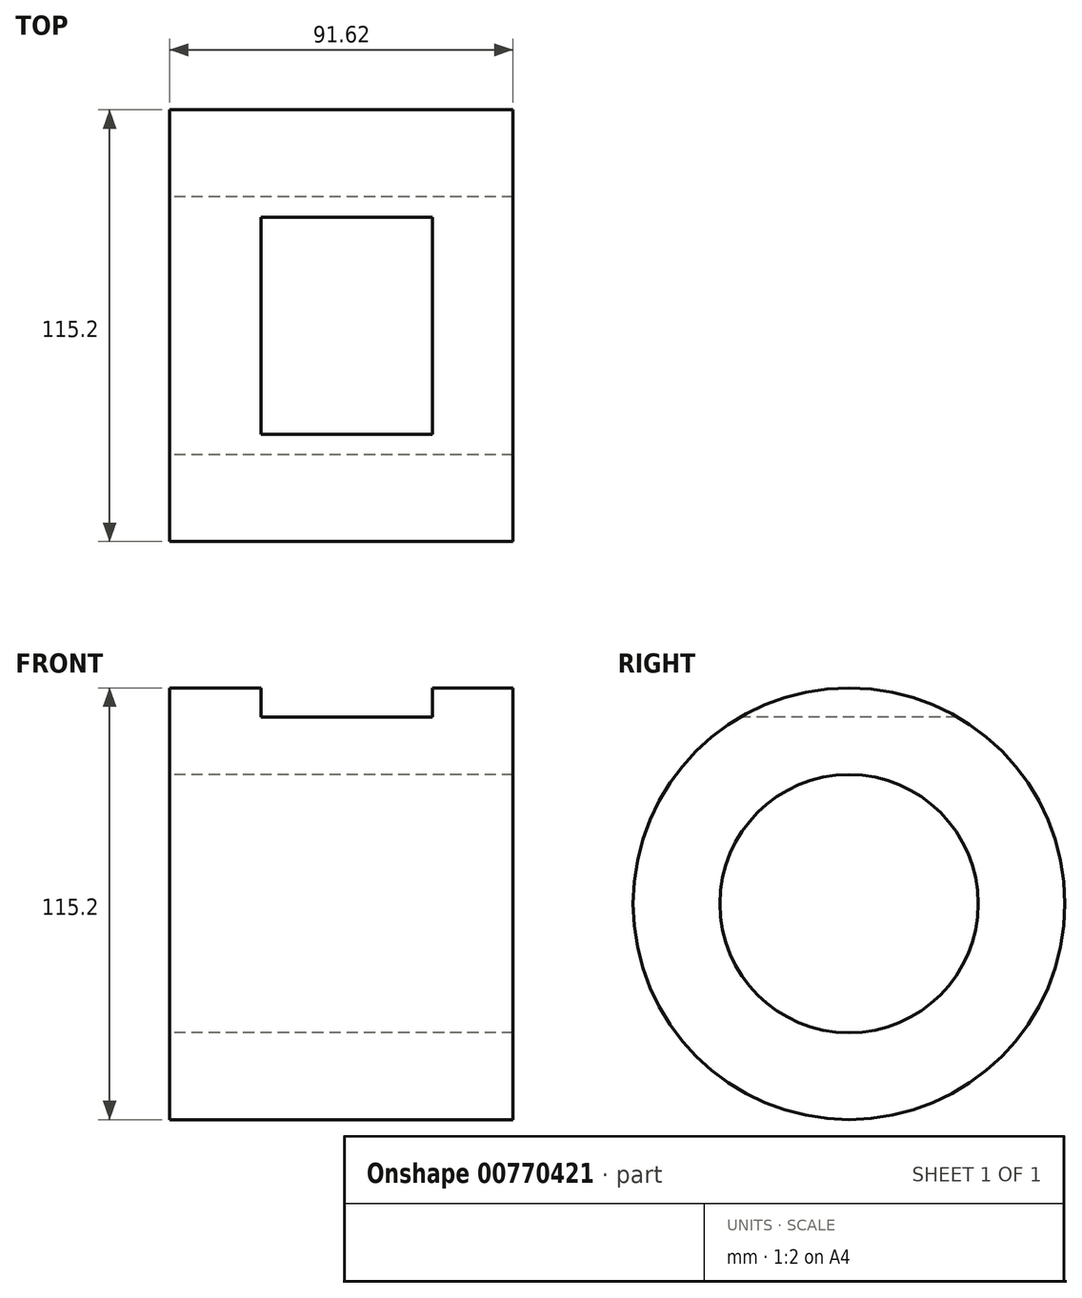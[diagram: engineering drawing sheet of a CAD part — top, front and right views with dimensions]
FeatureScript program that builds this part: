
annotation { "Feature Type Name" : "Feature", "Feature Type Description" : "" }
export const myFeature = defineFeature(function(context is Context, id is Id, definition is map)
    precondition{}
    {
        {
            var Q0;
            Q0=qCreatedBy(makeId("Front.planeOp"),FACE);
            var sketch = newSketch(context, id + "F0", { "sketchPlane" : qUnion([Q0])});
            skLineSegment(sketch, "E0", {"start": v(0, 0) * mm, "end": v(111.14, 0) * mm, "construction": true});
            skLineSegment(sketch, "E1.bottom", {"start": v(0, 57.6) * mm, "end": v(91.62, 57.6) * mm});
            skLineSegment(sketch, "E1.top", {"start": v(0, 34.44) * mm, "end": v(91.62, 34.44) * mm});
            skLineSegment(sketch, "E1.left", {"start": v(0, 57.6) * mm, "end": v(0, 34.44) * mm});
            skLineSegment(sketch, "E1.right", {"start": v(91.62, 57.6) * mm, "end": v(91.62, 34.44) * mm});
            skSolve(sketch);
        }
        {
            var Q0;
            Q0=makeQuery(id+"F0.imprint","IMPRINT",FACE,{"disambiguationData":[TD([[makeQuery(id+"F0.imprint","IMPRINT",EDGE,{"derivedFrom":sQuery(id+"F0.wireOp",EDGE,"E1.bottom")}),-1.0]])]});
            var Q1;
            Q1=sQuery(id+"F0.wireOp",EDGE,"E0");
            revolve(context, id + "F1", {"surfaceOperationType" : NewSurfaceOperationType.NEW, "entities" : qUnion([Q0]), "axis" : qUnion([Q1]), "revolveType" : RevolveType.FULL});
        }
        {
            var Q0;
            Q0=makeQuery(id+"F1.opRevolve","SWEPT_FACE",FACE,{"disambiguationData":[OSD([sQuery(id+"F0.wireOp",EDGE,"E1.right")])]});
            var sketch = newSketch(context, id + "F2", { "sketchPlane" : qUnion([Q0])});
            skLineSegment(sketch, "E2.bottom", {"start": v(-45.87, 62.11) * mm, "end": v(55.8, 62.11) * mm});
            skLineSegment(sketch, "E2.top", {"start": v(-45.87, 44.97) * mm, "end": v(55.8, 44.97) * mm});
            skLineSegment(sketch, "E2.left", {"start": v(-45.87, 62.11) * mm, "end": v(-45.87, 44.97) * mm});
            skLineSegment(sketch, "E2.right", {"start": v(55.8, 62.11) * mm, "end": v(55.8, 44.97) * mm});
            skSolve(sketch);
        }
        {
            var Q0;
            Q0=makeQuery(id+"F2.imprint","IMPRINT",FACE,{"disambiguationData":[TD([[makeQuery(id+"F2.imprint","IMPRINT",EDGE,{"derivedFrom":sQuery(id+"F2.wireOp",EDGE,"E2.bottom")}),-1.0]])]});
            extrude(context, id + "F3", {"entities" : qUnion([Q0]), "operationType" : NewBodyOperationType.REMOVE, "endBound" : BoundingType.THROUGH_ALL, "oppositeDirection" : true, "depth" : 25.4 * mm, "offsetDistance" : 25.4 * mm});
        }
        {
            var Q0;
            Q0=qCreatedBy(makeId("Front.planeOp"),FACE);
            var sketch = newSketch(context, id + "F4", { "sketchPlane" : qUnion([Q0])});
            skLineSegment(sketch, "E3.bottom", {"start": v(24.4, 65.42) * mm, "end": v(70.12, 65.42) * mm});
            skLineSegment(sketch, "E3.top", {"start": v(24.4, 49.78) * mm, "end": v(70.12, 49.78) * mm});
            skLineSegment(sketch, "E3.left", {"start": v(24.4, 65.42) * mm, "end": v(24.4, 49.78) * mm});
            skLineSegment(sketch, "E3.right", {"start": v(70.12, 65.42) * mm, "end": v(70.12, 49.78) * mm});
            skSolve(sketch);
        }
        {
            var Q0;
            Q0=makeQuery(id+"F4.imprint","IMPRINT",FACE,{"disambiguationData":[TD([[makeQuery(id+"F4.imprint","IMPRINT",EDGE,{"derivedFrom":sQuery(id+"F4.wireOp",EDGE,"E3.bottom")}),-1.0]])]});
            extrude(context, id + "F5", {"entities" : qUnion([Q0]), "operationType" : NewBodyOperationType.REMOVE, "endBound" : BoundingType.SYMMETRIC, "oppositeDirection" : true, "depth" : 76.2 * mm, "offsetDistance" : 25.4 * mm});
        }
    });
